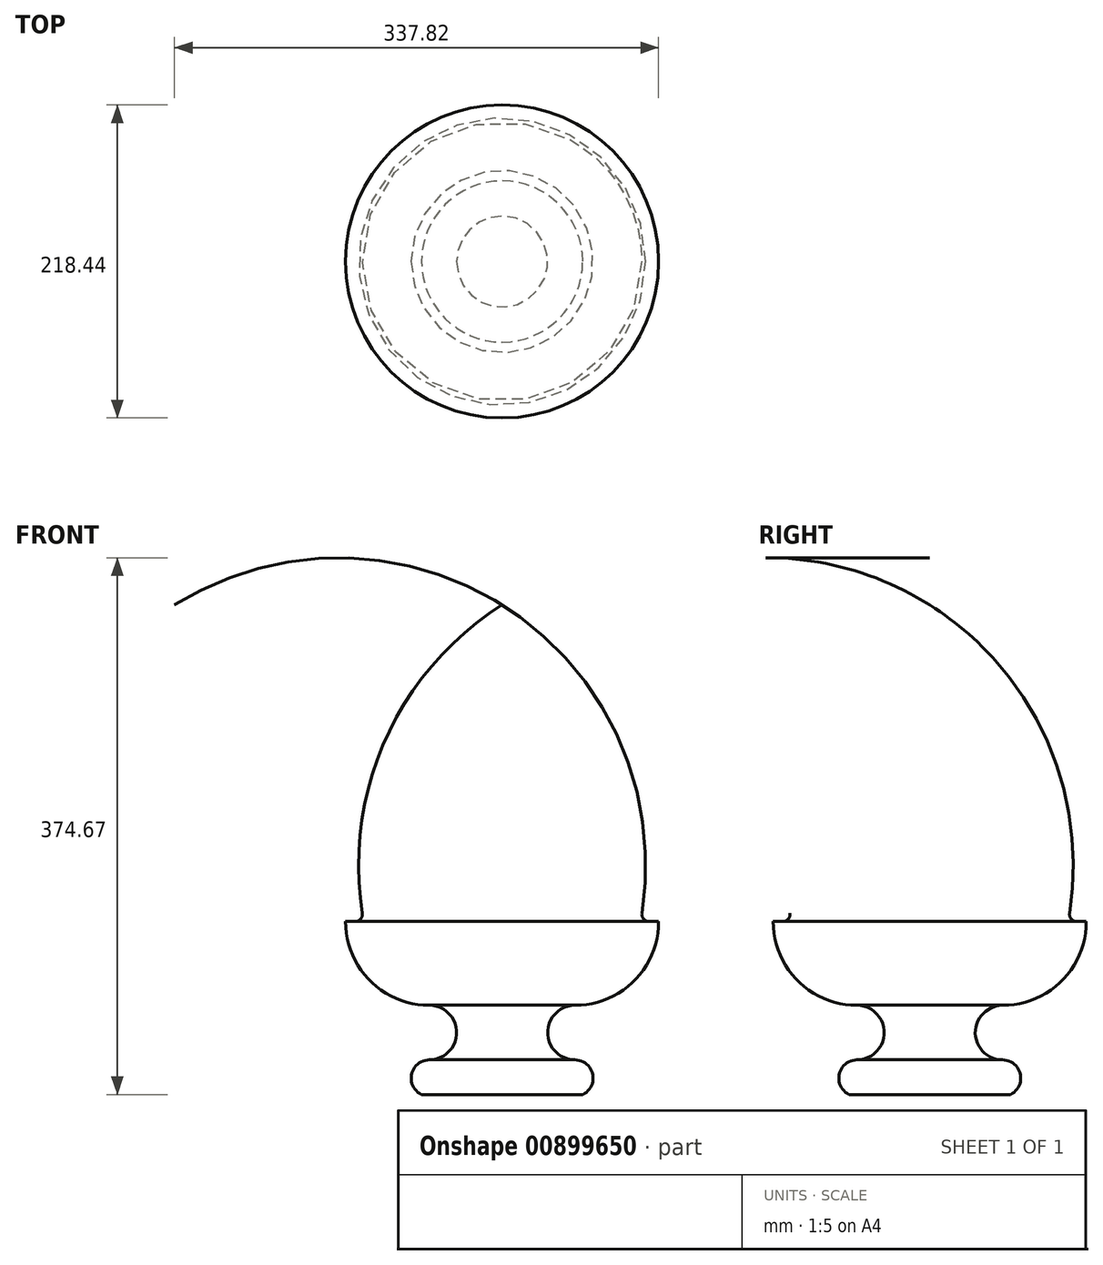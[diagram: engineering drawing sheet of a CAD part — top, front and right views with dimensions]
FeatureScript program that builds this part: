
annotation { "Feature Type Name" : "Feature", "Feature Type Description" : "" }
export const myFeature = defineFeature(function(context is Context, id is Id, definition is map)
    precondition{}
    {
        {
            var Q0;
            Q0=qCreatedBy(makeId("Top.planeOp"),FACE);
            var sketch = newSketch(context, id + "F0", { "sketchPlane" : qUnion([Q0])});
            skLineSegment(sketch, "E0.bottom", {"start": v(101.6, 101.6) * mm, "end": v(-101.6, 101.6) * mm});
            skLineSegment(sketch, "E0.top", {"start": v(101.6, -101.6) * mm, "end": v(-101.6, -101.6) * mm});
            skLineSegment(sketch, "E0.left", {"start": v(101.6, 101.6) * mm, "end": v(101.6, -101.6) * mm});
            skLineSegment(sketch, "E0.right", {"start": v(-101.6, 101.6) * mm, "end": v(-101.6, -101.6) * mm});
            skPoint(sketch, "E0.middle", {"position": v(0, 0) * mm});
            skSolve(sketch);
        }
        {
            var Q0;
            Q0=makeQuery(id+"F0.imprint","IMPRINT",FACE,{"disambiguationData":[TD([[makeQuery(id+"F0.imprint","IMPRINT",EDGE,{"derivedFrom":sQuery(id+"F0.wireOp",EDGE,"E0.bottom")}),1.0]])]});
            extrude(context, id + "F1", {"entities" : qUnion([Q0]), "depth" : 17.78 * mm, "offsetDistance" : 25.4 * mm});
        }
        {
            var Q0;
            Q0=qCreatedBy(makeId("Front.planeOp"),FACE);
            var sketch = newSketch(context, id + "F2", { "sketchPlane" : qUnion([Q0])});
            skLineSegment(sketch, "E1", {"start": v(0, 17.78) * mm, "end": v(0, 360.68) * mm});
            skArc(sketch, "E2", {"start": v(50.8, 81.28) * mm, "mid": v(92.1, 98.4) * mm, "end": v(109.22, 139.7) * mm});
            skArc(sketch, "E3", {"start": v(96.52, 139.7) * mm, "mid": v(82.25, 265.04) * mm, "end": v(0, 360.68) * mm});
            skLineSegment(sketch, "E4", {"start": v(109.22, 139.7) * mm, "end": v(96.52, 139.7) * mm});
            skArc(sketch, "E5", {"start": v(50.8, 17.78) * mm, "mid": v(63.5, 30.48) * mm, "end": v(50.8, 43.18) * mm});
            skArc(sketch, "E6", {"start": v(50.8, 81.28) * mm, "mid": v(31.75, 62.23) * mm, "end": v(50.8, 43.18) * mm});
            skLineSegment(sketch, "E7", {"start": v(0, 17.78) * mm, "end": v(50.8, 17.78) * mm});
            skPoint(sketch, "E8", {"position": v(71.13, 84.93) * mm});
            skPoint(sketch, "E9", {"position": v(81.8, 90.18) * mm});
            skPoint(sketch, "E10", {"position": v(92.1, 98.4) * mm});
            skPoint(sketch, "E11", {"position": v(99.58, 107.56) * mm});
            skPoint(sketch, "E12", {"position": v(106.22, 121.22) * mm});
            skPoint(sketch, "E13", {"position": v(108.74, 132.25) * mm});
            skSolve(sketch);
        }
        {
            var Q0;
            Q0=makeQuery(id+"F2.imprint","IMPRINT",FACE,{"disambiguationData":[TD([[makeQuery(id+"F2.imprint","IMPRINT",EDGE,{"derivedFrom":sQuery(id+"F2.wireOp",EDGE,"qheOzhUk-vern-bjLo-rjXj-7yKcvOgFfaP4")}),1.0]])]});
            var Q1;
            Q1=makeQuery(id+"F2.imprint","IMPRINT",FACE,{"disambiguationData":[TD([[makeQuery(id+"F2.imprint","IMPRINT",EDGE,{"derivedFrom":sQuery(id+"F2.wireOp",EDGE,"E1")}),-1.0]])]});
            var Q2;
            Q2=sQuery(id+"F2.wireOp",EDGE,"E1");
            revolve(context, id + "F3", {"operationType" : NewBodyOperationType.ADD, "surfaceOperationType" : NewSurfaceOperationType.NEW, "entities" : qUnion([Q0, Q1]), "axis" : qUnion([Q2]), "revolveType" : RevolveType.FULL});
        }
        {
            var Q0;
            Q0=makeQuery(id+"F3.opRevolve","SWEPT_EDGE",EDGE,{"disambiguationData":[OSD([sQuery(id+"F2.wireOp",EDGE,"E3"),sQuery(id+"F2.wireOp",EDGE,"E4")])]});
            fillet(context, id + "F4", {"entities" : qUnion([Q0]), "radius" : 5.08 * mm, "tangentPropagation" : true, "allowEdgeOverflow" : false});
        }
        {
            var Q0;
            Q0=makeQuery(id+"F1.opExtrude","CAP_FACE",FACE,{"disambiguationData":[OSD([sQuery(id+"F0.wireOp",EDGE,"E0.bottom"),sQuery(id+"F0.wireOp",EDGE,"E0.top"),sQuery(id+"F0.wireOp",EDGE,"E0.left"),sQuery(id+"F0.wireOp",EDGE,"E0.right")])],"isStart":true});
            var sketch = newSketch(context, id + "F5", { "sketchPlane" : qUnion([Q0])});
            skLineSegment(sketch, "E14.bottom", {"start": v(-101.6, 101.6) * mm, "end": v(101.6, 101.6) * mm});
            skLineSegment(sketch, "E14.top", {"start": v(-101.6, -101.6) * mm, "end": v(101.6, -101.6) * mm});
            skLineSegment(sketch, "E14.left", {"start": v(-101.6, 101.6) * mm, "end": v(-101.6, -101.6) * mm});
            skLineSegment(sketch, "E14.right", {"start": v(101.6, 101.6) * mm, "end": v(101.6, -101.6) * mm});
            skSolve(sketch);
        }
        {
            var Q0;
            Q0=makeQuery(id+"F5.imprint","IMPRINT",FACE,{"disambiguationData":[TD([[makeQuery(id+"F5.imprint","IMPRINT",EDGE,{"derivedFrom":sQuery(id+"F5.wireOp",EDGE,"E14.bottom")}),1.0]])]});
            extrude(context, id + "F6", {"entities" : qUnion([Q0]), "operationType" : NewBodyOperationType.REMOVE, "oppositeDirection" : true, "depth" : 19 * mm, "offsetDistance" : 25 * mm});
        }
    });
